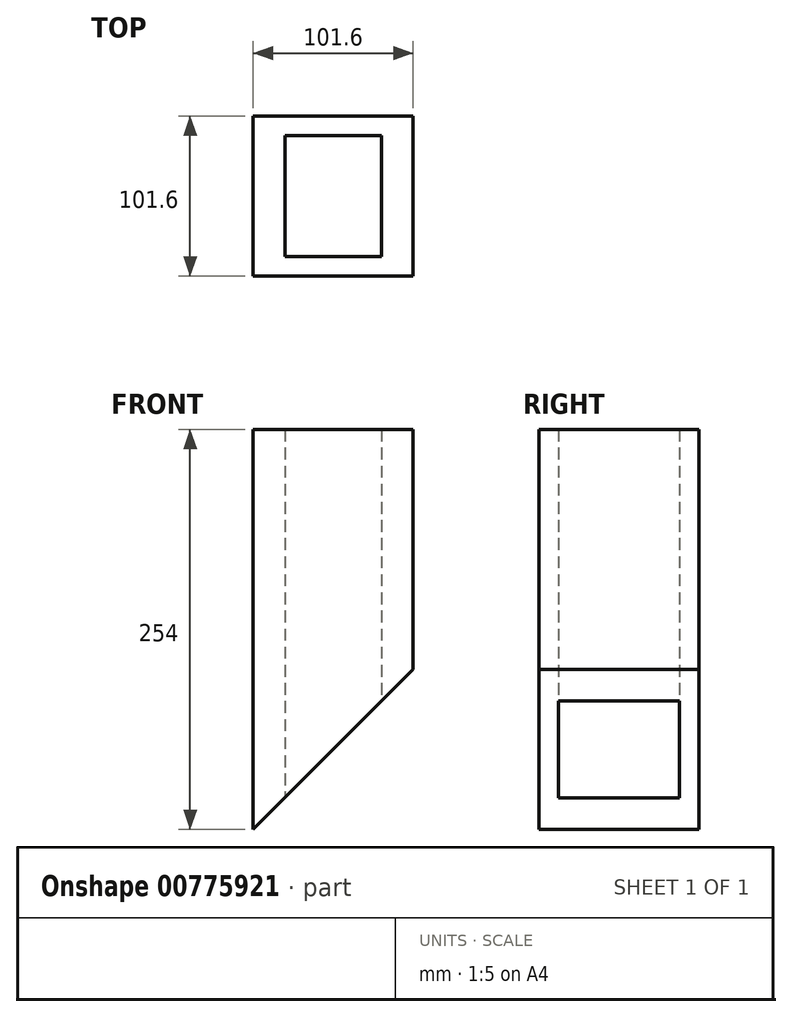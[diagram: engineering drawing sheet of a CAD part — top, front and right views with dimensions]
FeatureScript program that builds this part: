
annotation { "Feature Type Name" : "Feature", "Feature Type Description" : "" }
export const myFeature = defineFeature(function(context is Context, id is Id, definition is map)
    precondition{}
    {
        {
            var Q0;
            Q0=qCreatedBy(makeId("Top.planeOp"),FACE);
            var sketch = newSketch(context, id + "F0", { "sketchPlane" : qUnion([Q0])});
            skLineSegment(sketch, "E0.bottom", {"start": v(-23.81, 23.81) * mm, "end": v(23.81, 23.81) * mm});
            skLineSegment(sketch, "E0.top", {"start": v(-23.81, -23.81) * mm, "end": v(23.81, -23.81) * mm});
            skLineSegment(sketch, "E0.left", {"start": v(-23.81, 23.81) * mm, "end": v(-23.81, -23.81) * mm});
            skLineSegment(sketch, "E0.right", {"start": v(23.81, 23.81) * mm, "end": v(23.81, -23.81) * mm});
            skPoint(sketch, "E0.middle", {"position": v(0, 0) * mm});
            skLineSegment(sketch, "E1.bottom", {"start": v(-25.4, 25.4) * mm, "end": v(25.4, 25.4) * mm});
            skLineSegment(sketch, "E1.top", {"start": v(-25.4, -25.4) * mm, "end": v(25.4, -25.4) * mm});
            skLineSegment(sketch, "E1.left", {"start": v(-25.4, 25.4) * mm, "end": v(-25.4, -25.4) * mm});
            skLineSegment(sketch, "E1.right", {"start": v(25.4, 25.4) * mm, "end": v(25.4, -25.4) * mm});
            skSolve(sketch);
        }
        {
            var Q0;
            Q0=makeQuery(id+"F0.imprint","IMPRINT",FACE,{"disambiguationData":[TD([[makeQuery(id+"F0.imprint","IMPRINT",EDGE,{"derivedFrom":sQuery(id+"F0.wireOp",EDGE,"E0.bottom")}),1.0]])]});
            extrude(context, id + "F1", {"entities" : qUnion([Q0]), "depth" : 508 * mm, "offsetDistance" : 25.4 * mm});
        }
        {
            var Q0;
            Q0=makeQuery(id+"F1.opExtrude","SWEPT_FACE",FACE,{"disambiguationData":[OSD([sQuery(id+"F0.wireOp",EDGE,"E1.top")])]});
            var sketch = newSketch(context, id + "F2", { "sketchPlane" : qUnion([Q0])});
            skLineSegment(sketch, "E2", {"start": v(-25.4, 0) * mm, "end": v(25.4, 46) * mm});
            skSolve(sketch);
        }
        {
            var Q0;
            {var subQ0=sQuery(id+"F2.wireOp",EDGE,"E2");Q0=makeQuery(id+"F2.imprint","IMPRINT",FACE,{"disambiguationData":[TD([[makeQuery(id+"F2.imprint","IMPRINT",EDGE,{"derivedFrom":subQ0}),-1.0]])]});}
            extrude(context, id + "F3", {"entities" : qUnion([Q0]), "operationType" : NewBodyOperationType.REMOVE, "endBound" : BoundingType.THROUGH_ALL, "oppositeDirection" : true, "depth" : 25.4 * mm, "offsetDistance" : 25.4 * mm});
        }
        {
            var Q0;
            Q0=makeQuery(id+"F1.opExtrude","SWEPT_FACE",FACE,{"disambiguationData":[OSD([sQuery(id+"F0.wireOp",EDGE,"E1.top")])]});
            var sketch = newSketch(context, id + "F4", { "sketchPlane" : qUnion([Q0])});
            skLineSegment(sketch, "E3", {"start": v(-25.4, 508) * mm, "end": v(25.4, 469.43) * mm});
            skSolve(sketch);
        }
        {
            var Q0;
            {var subQ0=sQuery(id+"F4.wireOp",EDGE,"E3");Q0=makeQuery(id+"F4.imprint","IMPRINT",FACE,{"disambiguationData":[TD([[makeQuery(id+"F4.imprint","IMPRINT",EDGE,{"derivedFrom":subQ0}),1.0]])]});}
            extrude(context, id + "F5", {"entities" : qUnion([Q0]), "operationType" : NewBodyOperationType.REMOVE, "endBound" : BoundingType.THROUGH_ALL, "oppositeDirection" : true, "depth" : 25.4 * mm, "offsetDistance" : 25.4 * mm});
        }
        {
            var Q0;
            Q0=makeQuery(id+"F1.opExtrude","SWEPT_BODY",BODY,{"disambiguationData":[OSD([sQuery(id+"F0.wireOp",EDGE,"E0.bottom"),sQuery(id+"F0.wireOp",EDGE,"E0.top"),sQuery(id+"F0.wireOp",EDGE,"E0.left"),sQuery(id+"F0.wireOp",EDGE,"E0.right"),sQuery(id+"F0.wireOp",EDGE,"E1.bottom"),sQuery(id+"F0.wireOp",EDGE,"E1.top"),sQuery(id+"F0.wireOp",EDGE,"E1.left"),sQuery(id+"F0.wireOp",EDGE,"E1.right")])]});
            deleteBodies(context, id + "F6", {"entities" : qUnion([Q0])});
        }
        {
            var Q0;
            Q0=qCreatedBy(makeId("Top.planeOp"),FACE);
            var sketch = newSketch(context, id + "F7", { "sketchPlane" : qUnion([Q0])});
            skLineSegment(sketch, "E4.bottom", {"start": v(-30.69, 38.5) * mm, "end": v(30.69, 38.5) * mm});
            skLineSegment(sketch, "E4.top", {"start": v(-30.69, -38.5) * mm, "end": v(30.69, -38.5) * mm});
            skLineSegment(sketch, "E4.left", {"start": v(-30.69, 38.5) * mm, "end": v(-30.69, -38.5) * mm});
            skLineSegment(sketch, "E4.right", {"start": v(30.69, 38.5) * mm, "end": v(30.69, -38.5) * mm});
            skPoint(sketch, "E4.middle", {"position": v(0, 0) * mm});
            skLineSegment(sketch, "E5.bottom", {"start": v(-50.8, 50.8) * mm, "end": v(50.8, 50.8) * mm});
            skLineSegment(sketch, "E5.top", {"start": v(-50.8, -50.8) * mm, "end": v(50.8, -50.8) * mm});
            skLineSegment(sketch, "E5.left", {"start": v(-50.8, 50.8) * mm, "end": v(-50.8, -50.8) * mm});
            skLineSegment(sketch, "E5.right", {"start": v(50.8, 50.8) * mm, "end": v(50.8, -50.8) * mm});
            skSolve(sketch);
        }
        {
            var Q0;
            Q0=makeQuery(id+"F7.imprint","IMPRINT",FACE,{"disambiguationData":[TD([[makeQuery(id+"F7.imprint","IMPRINT",EDGE,{"derivedFrom":sQuery(id+"F7.wireOp",EDGE,"E4.bottom")}),1.0]])]});
            extrude(context, id + "F8", {"entities" : qUnion([Q0]), "depth" : 254 * mm, "offsetDistance" : 25.4 * mm});
        }
        {
            var Q0;
            Q0=makeQuery(id+"F8.opExtrude","SWEPT_FACE",FACE,{"disambiguationData":[OSD([sQuery(id+"F7.wireOp",EDGE,"E5.top")])]});
            var sketch = newSketch(context, id + "F9", { "sketchPlane" : qUnion([Q0])});
            skLineSegment(sketch, "E6", {"start": v(-50.8, 0) * mm, "end": v(50.8, 101.6) * mm});
            skSolve(sketch);
        }
        {
            var Q0;
            {var subQ0=sQuery(id+"F9.wireOp",EDGE,"E6");Q0=makeQuery(id+"F9.imprint","IMPRINT",FACE,{"disambiguationData":[TD([[makeQuery(id+"F9.imprint","IMPRINT",EDGE,{"derivedFrom":subQ0}),-1.0]])]});}
            extrude(context, id + "F10", {"entities" : qUnion([Q0]), "operationType" : NewBodyOperationType.REMOVE, "endBound" : BoundingType.THROUGH_ALL, "oppositeDirection" : true, "depth" : 25.4 * mm, "offsetDistance" : 25.4 * mm});
        }
    });
